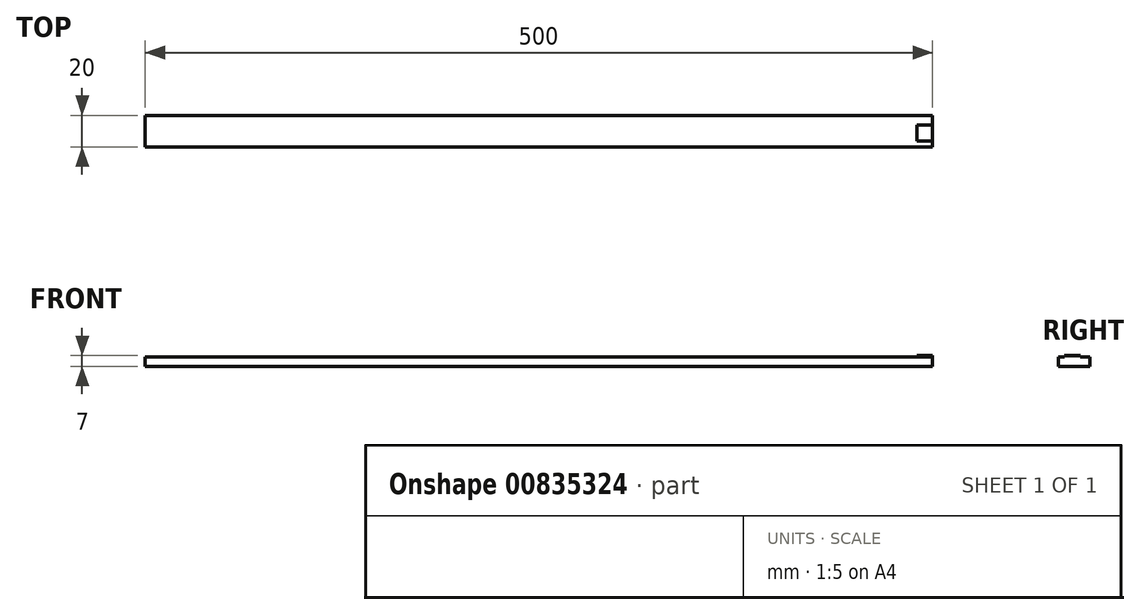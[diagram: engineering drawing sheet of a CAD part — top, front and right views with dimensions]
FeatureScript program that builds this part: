
annotation { "Feature Type Name" : "Feature", "Feature Type Description" : "" }
export const myFeature = defineFeature(function(context is Context, id is Id, definition is map)
    precondition{}
    {
        {
            var Q0;
            Q0=qCreatedBy(makeId("Top.planeOp"),FACE);
            var sketch = newSketch(context, id + "F0", { "sketchPlane" : qUnion([Q0])});
            skLineSegment(sketch, "E0.bottom", {"start": v(-237.57, -69.66) * mm, "end": v(262.43, -69.66) * mm});
            skLineSegment(sketch, "E0.left", {"start": v(-237.57, -69.66) * mm, "end": v(-237.57, -79.66) * mm});
            skLineSegment(sketch, "E1.MirrorCS", {"start": v(-237.57, -89.66) * mm, "end": v(262.43, -89.66) * mm});
            skLineSegment(sketch, "E2", {"start": v(-237.57, -89.66) * mm, "end": v(-237.57, -79.66) * mm});
            skLineSegment(sketch, "E3", {"start": v(262.43, -69.66) * mm, "end": v(262.43, -89.66) * mm});
            skSolve(sketch);
        }
        {
            var Q0;
            Q0=makeQuery(id+"F0.imprint","IMPRINT",FACE,{"disambiguationData":[TD([[makeQuery(id+"F0.imprint","IMPRINT",EDGE,{"derivedFrom":sQuery(id+"F0.wireOp",EDGE,"E0.bottom")}),-1.0]])]});
            extrude(context, id + "F1", {"entities" : qUnion([Q0]), "depth" : 6 * mm, "offsetDistance" : 25 * mm});
        }
        {
            var Q0;
            Q0=makeQuery(id+"F1.opExtrude","CAP_FACE",FACE,{"disambiguationData":[OSD([sQuery(id+"F0.wireOp",EDGE,"E0.bottom"),sQuery(id+"F0.wireOp",EDGE,"E0.left"),sQuery(id+"F0.wireOp",EDGE,"E1.MirrorCS"),sQuery(id+"F0.wireOp",EDGE,"E2"),sQuery(id+"F0.wireOp",EDGE,"E3")])],"isStart":false});
            var sketch = newSketch(context, id + "F2", { "sketchPlane" : qUnion([Q0])});
            skLineSegment(sketch, "E4.bottom", {"start": v(262.58, -75.8) * mm, "end": v(252.58, -75.8) * mm});
            skLineSegment(sketch, "E4.top", {"start": v(262.58, -85.8) * mm, "end": v(252.58, -85.8) * mm});
            skLineSegment(sketch, "E4.left", {"start": v(262.58, -75.8) * mm, "end": v(262.58, -85.8) * mm});
            skLineSegment(sketch, "E4.right", {"start": v(252.58, -75.8) * mm, "end": v(252.58, -85.8) * mm});
            skSolve(sketch);
        }
        {
            var Q0;
            {var subQ0=sQuery(id+"F2.wireOp",EDGE,"E4.right");Q0=makeQuery(id+"F2.imprint","IMPRINT",FACE,{"disambiguationData":[TD([[makeQuery(id+"F2.imprint","IMPRINT",EDGE,{"derivedFrom":subQ0}),1.0]])]});}
            extrude(context, id + "F3", {"entities" : qUnion([Q0]), "operationType" : NewBodyOperationType.ADD, "depth" : 1 * mm, "offsetDistance" : 25 * mm});
        }
    });
